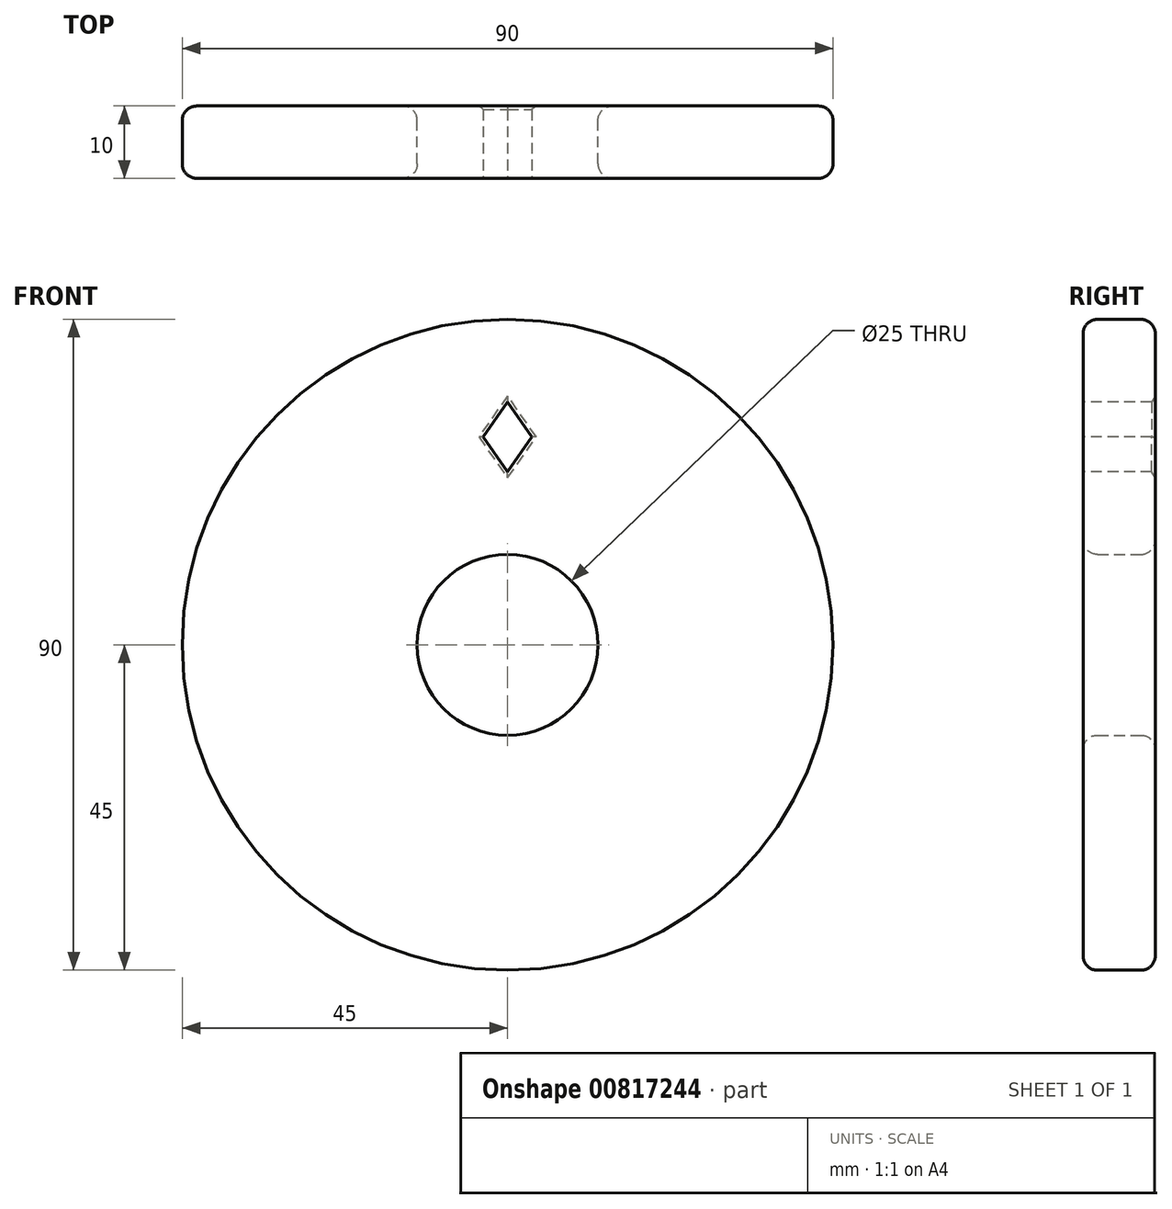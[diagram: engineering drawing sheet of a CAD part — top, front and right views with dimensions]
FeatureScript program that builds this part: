
annotation { "Feature Type Name" : "Feature", "Feature Type Description" : "" }
export const myFeature = defineFeature(function(context is Context, id is Id, definition is map)
    precondition{}
    {
        {
            var Q0;
            Q0=qCreatedBy(makeId("Front.planeOp"),FACE);
            var sketch = newSketch(context, id + "F0", { "sketchPlane" : qUnion([Q0])});
            skCircle(sketch, "E0", {"center": v(0, 0) * mm, "radius": 45 * mm});
            skCircle(sketch, "E1", {"center": v(0, 0) * mm, "radius": 12.5 * mm});
            skSolve(sketch);
        }
        {
            var Q0;
            Q0=makeQuery(id+"F0.imprint","IMPRINT",FACE,{"disambiguationData":[TD([[makeQuery(id+"F0.imprint","IMPRINT",EDGE,{"derivedFrom":sQuery(id+"F0.wireOp",EDGE,"E0")}),1.0]])]});
            extrude(context, id + "F1", {"entities" : qUnion([Q0]), "depth" : 10 * mm, "offsetDistance" : 25 * mm, "symmetric" : true});
        }
        {
            var Q0;
            Q0=makeQuery(id+"F1.opExtrude","CAP_FACE",FACE,{"disambiguationData":[OSD([sQuery(id+"F0.wireOp",EDGE,"E0"),sQuery(id+"F0.wireOp",EDGE,"E1")])],"isStart":false});
            var sketch = newSketch(context, id + "F2", { "sketchPlane" : qUnion([Q0])});
            skCircle(sketch, "E2", {"center": v(0, 0) * mm, "radius": 28.75 * mm, "construction": true});
            skLineSegment(sketch, "E3", {"start": v(0, 33.55) * mm, "end": v(-3.36, 28.75) * mm});
            skLineSegment(sketch, "E4", {"start": v(-3.36, 28.75) * mm, "end": v(0, 23.95) * mm});
            skLineSegment(sketch, "E5", {"start": v(0, 33.55) * mm, "end": v(3.36, 28.75) * mm});
            skLineSegment(sketch, "E6", {"start": v(3.36, 28.75) * mm, "end": v(0, 23.95) * mm});
            skLineSegment(sketch, "E7", {"start": v(0, 28.75) * mm, "end": v(0, 33.55) * mm, "construction": true});
            skLineSegment(sketch, "E8", {"start": v(0, 28.75) * mm, "end": v(0, 23.95) * mm, "construction": true});
            skLineSegment(sketch, "E9", {"start": v(0, 28.75) * mm, "end": v(-3.36, 28.75) * mm, "construction": true});
            skLineSegment(sketch, "E10", {"start": v(0, 28.75) * mm, "end": v(3.36, 28.75) * mm, "construction": true});
            skSolve(sketch);
        }
        {
            var Q0;
            Q0 = qSketchRegion(id + "F2", true);
            extrude(context, id + "F3", {"entities" : qUnion([Q0]), "operationType" : NewBodyOperationType.REMOVE, "endBound" : BoundingType.THROUGH_ALL, "oppositeDirection" : true, "depth" : 25 * mm, "offsetDistance" : 25 * mm});
        }
        {
            var Q0;
            Q0=makeQuery(id+"F3.boolean.opBoolean","COPY",EDGE,{"derivedFrom":makeQuery(id+"F3.opExtrude","CAP_EDGE",EDGE,{"disambiguationData":[OSD([sQuery(id+"F2.wireOp",EDGE,"E5")])],"isStart":true})});
            var Q1;
            Q1=makeQuery(id+"F3.boolean.opBoolean","COPY",EDGE,{"derivedFrom":makeQuery(id+"F3.opExtrude","CAP_EDGE",EDGE,{"disambiguationData":[OSD([sQuery(id+"F2.wireOp",EDGE,"E3")])],"isStart":true})});
            var Q2;
            Q2=makeQuery(id+"F3.boolean.opBoolean","COPY",EDGE,{"derivedFrom":makeQuery(id+"F3.opExtrude","CAP_EDGE",EDGE,{"disambiguationData":[OSD([sQuery(id+"F2.wireOp",EDGE,"E4")])],"isStart":true})});
            var Q3;
            Q3=makeQuery(id+"F3.boolean.opBoolean","COPY",EDGE,{"derivedFrom":makeQuery(id+"F3.opExtrude","CAP_EDGE",EDGE,{"disambiguationData":[OSD([sQuery(id+"F2.wireOp",EDGE,"E6")])],"isStart":true})});
            var Q4;
            Q4=makeQuery(id+"F3.boolean.opBoolean","INTERSECT",EDGE,{"derivedFrom":[makeQuery(id+"F1.opExtrude","CAP_FACE",FACE,{"disambiguationData":[OSD([sQuery(id+"F0.wireOp",EDGE,"E0"),sQuery(id+"F0.wireOp",EDGE,"E1")])],"isStart":true}),makeQuery(id+"F3.opExtrude","SWEPT_FACE",FACE,{"disambiguationData":[OSD([sQuery(id+"F2.wireOp",EDGE,"E5")])]})]});
            var Q5;
            Q5=makeQuery(id+"F3.boolean.opBoolean","INTERSECT",EDGE,{"derivedFrom":[makeQuery(id+"F1.opExtrude","CAP_FACE",FACE,{"disambiguationData":[OSD([sQuery(id+"F0.wireOp",EDGE,"E0"),sQuery(id+"F0.wireOp",EDGE,"E1")])],"isStart":true}),makeQuery(id+"F3.opExtrude","SWEPT_FACE",FACE,{"disambiguationData":[OSD([sQuery(id+"F2.wireOp",EDGE,"E3")])]})]});
            var Q6;
            Q6=makeQuery(id+"F3.boolean.opBoolean","INTERSECT",EDGE,{"derivedFrom":[makeQuery(id+"F1.opExtrude","CAP_FACE",FACE,{"disambiguationData":[OSD([sQuery(id+"F0.wireOp",EDGE,"E0"),sQuery(id+"F0.wireOp",EDGE,"E1")])],"isStart":true}),makeQuery(id+"F3.opExtrude","SWEPT_FACE",FACE,{"disambiguationData":[OSD([sQuery(id+"F2.wireOp",EDGE,"E4")])]})]});
            var Q7;
            Q7=makeQuery(id+"F3.boolean.opBoolean","INTERSECT",EDGE,{"derivedFrom":[makeQuery(id+"F1.opExtrude","CAP_FACE",FACE,{"disambiguationData":[OSD([sQuery(id+"F0.wireOp",EDGE,"E0"),sQuery(id+"F0.wireOp",EDGE,"E1")])],"isStart":true}),makeQuery(id+"F3.opExtrude","SWEPT_FACE",FACE,{"disambiguationData":[OSD([sQuery(id+"F2.wireOp",EDGE,"E6")])]})]});
            chamfer(context, id + "F4", {"entities" : qUnion([Q0, Q1, Q2, Q3, Q4, Q5, Q6, Q7]), "width" : 0.5 * mm, "tangentPropagation" : true});
        }
        {
            var Q0;
            Q0=makeQuery(id+"F1.opExtrude","CAP_EDGE",EDGE,{"disambiguationData":[OSD([sQuery(id+"F0.wireOp",EDGE,"E0")])],"isStart":false});
            var Q1;
            Q1=makeQuery(id+"F1.opExtrude","CAP_EDGE",EDGE,{"disambiguationData":[OSD([sQuery(id+"F0.wireOp",EDGE,"E0")])],"isStart":true});
            var Q2;
            Q2=makeQuery(id+"F1.opExtrude","SWEPT_FACE",FACE,{"disambiguationData":[OSD([sQuery(id+"F0.wireOp",EDGE,"E1")])]});
            fillet(context, id + "F5", {"entities" : qUnion([Q0, Q1, Q2]), "radius" : 2 * mm, "tangentPropagation" : true, "allowEdgeOverflow" : false});
        }
    });
